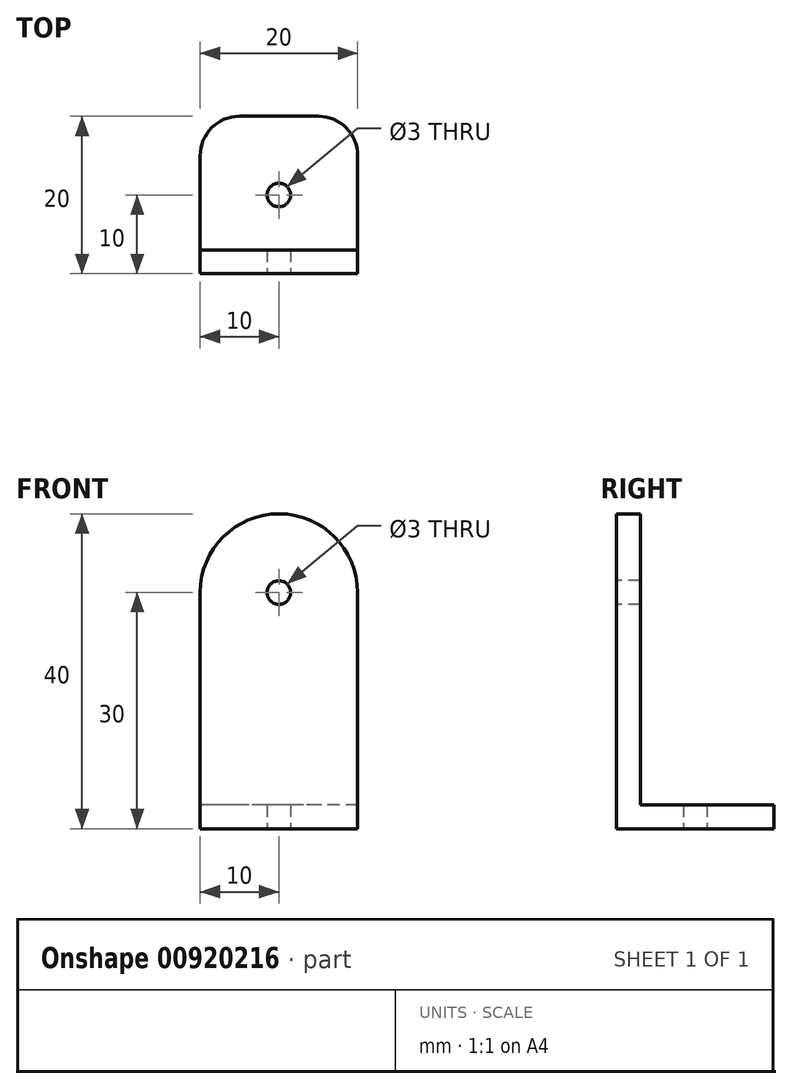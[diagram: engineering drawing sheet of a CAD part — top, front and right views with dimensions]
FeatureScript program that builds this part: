
annotation { "Feature Type Name" : "Feature", "Feature Type Description" : "" }
export const myFeature = defineFeature(function(context is Context, id is Id, definition is map)
    precondition{}
    {
        {
            var Q0;
            Q0=qCreatedBy(makeId("Top.planeOp"),FACE);
            var sketch = newSketch(context, id + "F0", { "sketchPlane" : qUnion([Q0])});
            skLineSegment(sketch, "E0.bottom", {"start": v(5, 10) * mm, "end": v(-5, 10) * mm});
            skLineSegment(sketch, "E0.top", {"start": v(10, -10) * mm, "end": v(-10, -10) * mm});
            skLineSegment(sketch, "E0.left", {"start": v(10, 5) * mm, "end": v(10, -10) * mm});
            skLineSegment(sketch, "E0.right", {"start": v(-10, 5) * mm, "end": v(-10, -10) * mm});
            skPoint(sketch, "E0.middle", {"position": v(0, 0) * mm});
            skCircle(sketch, "E1", {"center": v(0, 0) * mm, "radius": 1.5 * mm});
            skPoint(sketch, "E2.visualSharp", {"position": v(-10, 10) * mm});
            skArc(sketch, "E2.filletArc", {"start": v(-5, 10) * mm, "mid": v(-8.54, 8.54) * mm, "end": v(-10, 5) * mm});
            skPoint(sketch, "E3.visualSharp", {"position": v(10, 10) * mm});
            skArc(sketch, "E3.filletArc", {"start": v(10, 5) * mm, "mid": v(8.54, 8.54) * mm, "end": v(5, 10) * mm});
            skSolve(sketch);
        }
        {
            var Q0;
            Q0 = qSketchRegion(id + "F0", true);
            extrude(context, id + "F1", {"entities" : qUnion([Q0]), "depth" : 3 * mm, "offsetDistance" : 25 * mm});
        }
        {
            var Q0;
            Q0=makeQuery(id+"F1.opExtrude","SWEPT_FACE",FACE,{"disambiguationData":[OSD([sQuery(id+"F0.wireOp",EDGE,"E0.top")])]});
            var sketch = newSketch(context, id + "F2", { "sketchPlane" : qUnion([Q0])});
            skLineSegment(sketch, "E4.bottom", {"start": v(-10, 0) * mm, "end": v(10, 0) * mm});
            skLineSegment(sketch, "E4.left", {"start": v(-10, 0) * mm, "end": v(-10, 30) * mm});
            skLineSegment(sketch, "E4.right", {"start": v(10, 0) * mm, "end": v(10, 30) * mm});
            skArc(sketch, "E5", {"start": v(10, 30) * mm, "mid": v(0, 40) * mm, "end": v(-10, 30) * mm});
            skCircle(sketch, "E6", {"center": v(0, 30) * mm, "radius": 1.5 * mm});
            skSolve(sketch);
        }
        {
            var Q0;
            {var subQ0=sQuery(id+"F2.wireOp",EDGE,"E5");Q0=makeQuery(id+"F2.imprint","IMPRINT",FACE,{"disambiguationData":[TD([[makeQuery(id+"F2.imprint","IMPRINT",EDGE,{"derivedFrom":subQ0}),1.0]])]});}
            extrude(context, id + "F3", {"entities" : qUnion([Q0]), "operationType" : NewBodyOperationType.ADD, "depth" : -3 * mm, "offsetDistance" : 25 * mm});
        }
    });
